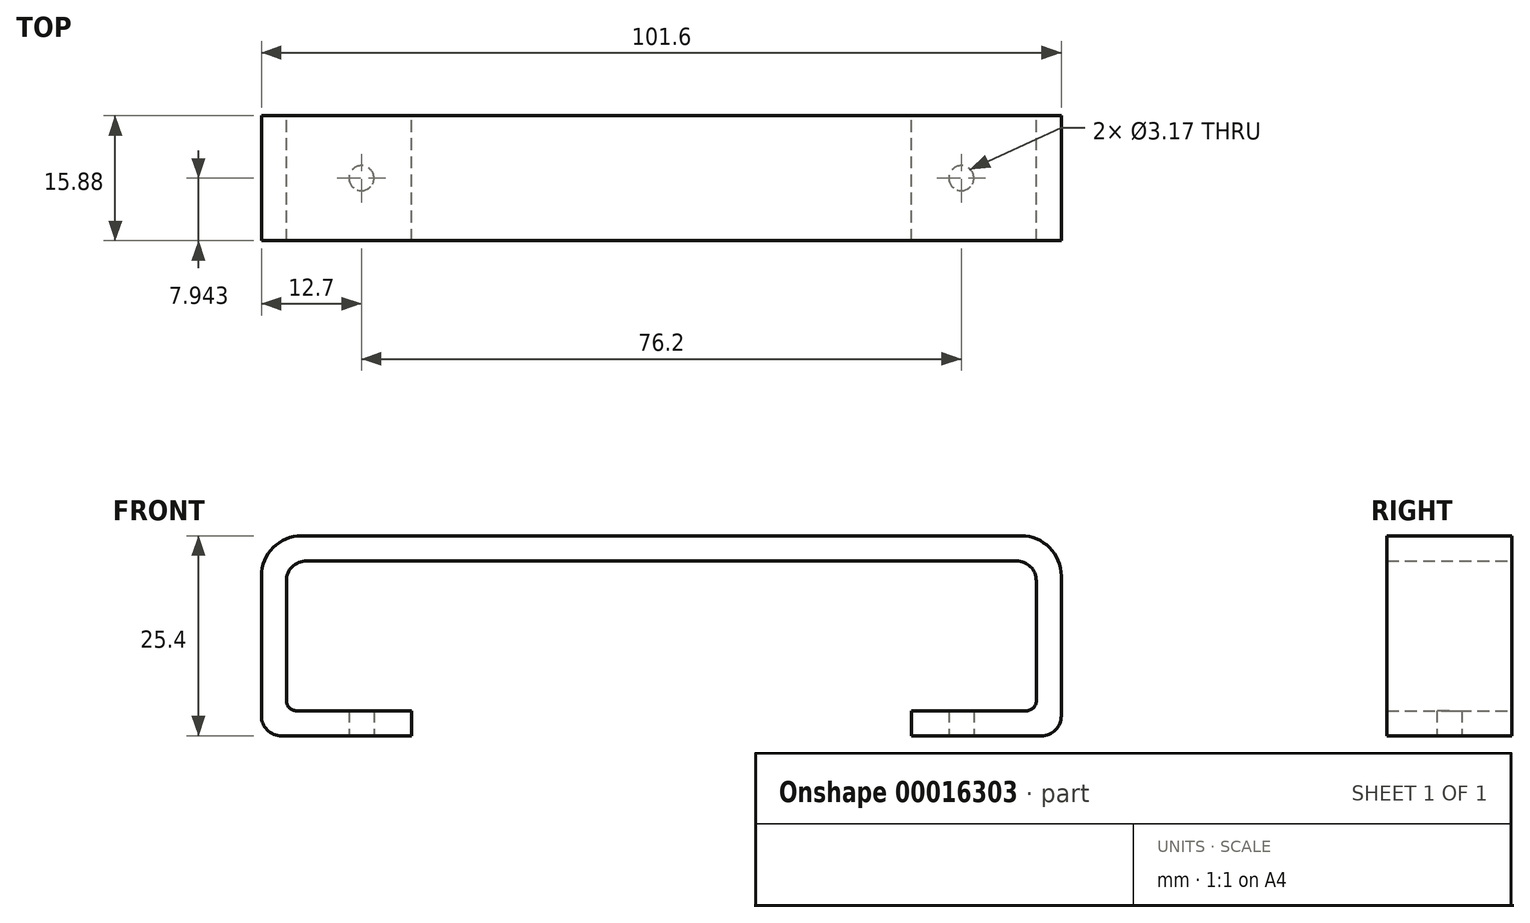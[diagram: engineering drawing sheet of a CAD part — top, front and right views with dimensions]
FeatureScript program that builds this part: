
annotation { "Feature Type Name" : "Feature", "Feature Type Description" : "" }
export const myFeature = defineFeature(function(context is Context, id is Id, definition is map)
    precondition{}
    {
        {
            var Q0;
            Q0=qCreatedBy(makeId("Front.planeOp"),FACE);
            var sketch = newSketch(context, id + "F0", { "sketchPlane" : qUnion([Q0])});
            skLineSegment(sketch, "E0.bottom", {"start": v(0, 0) * mm, "end": v(19.05, 0) * mm});
            skLineSegment(sketch, "E0.top", {"start": v(0, 25.4) * mm, "end": v(101.6, 25.4) * mm});
            skLineSegment(sketch, "E0.left", {"start": v(0, 0) * mm, "end": v(0, 25.4) * mm});
            skLineSegment(sketch, "E0.right", {"start": v(101.6, 0) * mm, "end": v(101.6, 25.4) * mm});
            skLineSegment(sketch, "E1.0", {"start": v(3.17, 3.18) * mm, "end": v(3.17, 22.23) * mm});
            skLineSegment(sketch, "E2.0", {"start": v(3.17, 22.23) * mm, "end": v(98.43, 22.23) * mm});
            skLineSegment(sketch, "E3.0", {"start": v(98.43, 0) * mm, "end": v(98.43, 22.23) * mm});
            skLineSegment(sketch, "E4.0", {"start": v(3.18, 3.18) * mm, "end": v(19.05, 3.18) * mm});
            skLineSegment(sketch, "E5", {"start": v(19.05, 0) * mm, "end": v(19.05, 3.17) * mm});
            skLineSegment(sketch, "E6.0", {"start": v(82.55, 0) * mm, "end": v(82.55, 3.17) * mm});
            skLineSegment(sketch, "E7.trimOffspring", {"start": v(82.55, 0) * mm, "end": v(101.6, 0) * mm});
            skLineSegment(sketch, "E8.trimOffspring", {"start": v(82.55, 3.18) * mm, "end": v(98.43, 3.18) * mm});
            skSolve(sketch);
        }
        {
            var Q0;
            Q0 = qSketchRegion(id + "F0", true);
            extrude(context, id + "F1", {"entities" : qUnion([Q0]), "depth" : 15.88 * mm});
        }
        {
            var Q0;
            Q0=makeQuery(id+"F1.opExtrude","SWEPT_EDGE",EDGE,{"disambiguationData":[OSD([sQuery(id+"F0.wireOp",EDGE,"E0.top"),sQuery(id+"F0.wireOp",EDGE,"E0.left")])]});
            var Q1;
            Q1=makeQuery(id+"F1.opExtrude","SWEPT_EDGE",EDGE,{"disambiguationData":[OSD([sQuery(id+"F0.wireOp",EDGE,"E0.top"),sQuery(id+"F0.wireOp",EDGE,"E0.right")])]});
            fillet(context, id + "F2", {"entities" : qUnion([Q0, Q1]), "radius" : 5.08 * mm, "tangentPropagation" : true, "allowEdgeOverflow" : false});
        }
        {
            var Q0;
            Q0=makeQuery(id+"F1.opExtrude","SWEPT_EDGE",EDGE,{"disambiguationData":[OSD([sQuery(id+"F0.wireOp",EDGE,"E1.0"),sQuery(id+"F0.wireOp",EDGE,"E2.0")])]});
            fillet(context, id + "F3", {"entities" : qUnion([Q0]), "radius" : 2.54 * mm, "tangentPropagation" : true, "allowEdgeOverflow" : false});
        }
        {
            var Q0;
            Q0=makeQuery(id+"F1.opExtrude","SWEPT_EDGE",EDGE,{"disambiguationData":[OSD([sQuery(id+"F0.wireOp",EDGE,"E2.0"),sQuery(id+"F0.wireOp",EDGE,"E3.0")])]});
            fillet(context, id + "F4", {"entities" : qUnion([Q0]), "radius" : 2.54 * mm, "tangentPropagation" : true, "allowEdgeOverflow" : false});
        }
        {
            var Q0;
            Q0=makeQuery(id+"F1.opExtrude","SWEPT_EDGE",EDGE,{"disambiguationData":[OSD([sQuery(id+"F0.wireOp",EDGE,"E0.bottom"),sQuery(id+"F0.wireOp",EDGE,"E0.left")])]});
            fillet(context, id + "F5", {"entities" : qUnion([Q0]), "radius" : 2.54 * mm, "tangentPropagation" : true, "allowEdgeOverflow" : false});
        }
        {
            var Q0;
            Q0=makeQuery(id+"F1.opExtrude","SWEPT_EDGE",EDGE,{"disambiguationData":[OSD([sQuery(id+"F0.wireOp",EDGE,"E0.right"),sQuery(id+"F0.wireOp",EDGE,"E7.trimOffspring")])]});
            fillet(context, id + "F6", {"entities" : qUnion([Q0]), "radius" : 2.54 * mm, "tangentPropagation" : true, "allowEdgeOverflow" : false});
        }
        {
            var Q0;
            Q0=makeQuery(id+"F1.opExtrude","SWEPT_EDGE",EDGE,{"disambiguationData":[OSD([sQuery(id+"F0.wireOp",EDGE,"E1.0"),sQuery(id+"F0.wireOp",EDGE,"E4.0")])]});
            var Q1;
            Q1=makeQuery(id+"F1.opExtrude","SWEPT_EDGE",EDGE,{"disambiguationData":[OSD([sQuery(id+"F0.wireOp",EDGE,"E3.0"),sQuery(id+"F0.wireOp",EDGE,"E8.trimOffspring")])]});
            fillet(context, id + "F7", {"entities" : qUnion([Q0, Q1]), "radius" : 1.27 * mm, "tangentPropagation" : true, "allowEdgeOverflow" : false});
        }
        {
            var Q0;
            Q0=makeQuery(id+"F1.opExtrude","SWEPT_FACE",FACE,{"disambiguationData":[OSD([sQuery(id+"F0.wireOp",EDGE,"E0.bottom")])]});
            var sketch = newSketch(context, id + "F8", { "sketchPlane" : qUnion([Q0])});
            skCircle(sketch, "E9", {"center": v(12.7, 7.94) * mm, "radius": 1.59 * mm});
            skPoint(sketch, "E9.centerSnap0", {"position": v(19.05, 7.94) * mm});
            skCircle(sketch, "E10.MirrorC", {"center": v(88.9, 7.94) * mm, "radius": 1.59 * mm});
            skPoint(sketch, "E11.end.orphan", {"position": v(50.8, 0) * mm});
            skSolve(sketch);
        }
        {
            var Q0;
            Q0 = qSketchRegion(id + "F8", true);
            extrude(context, id + "F9", {"entities" : qUnion([Q0]), "operationType" : NewBodyOperationType.REMOVE, "oppositeDirection" : true, "depth" : 6.35 * mm});
        }
    });
